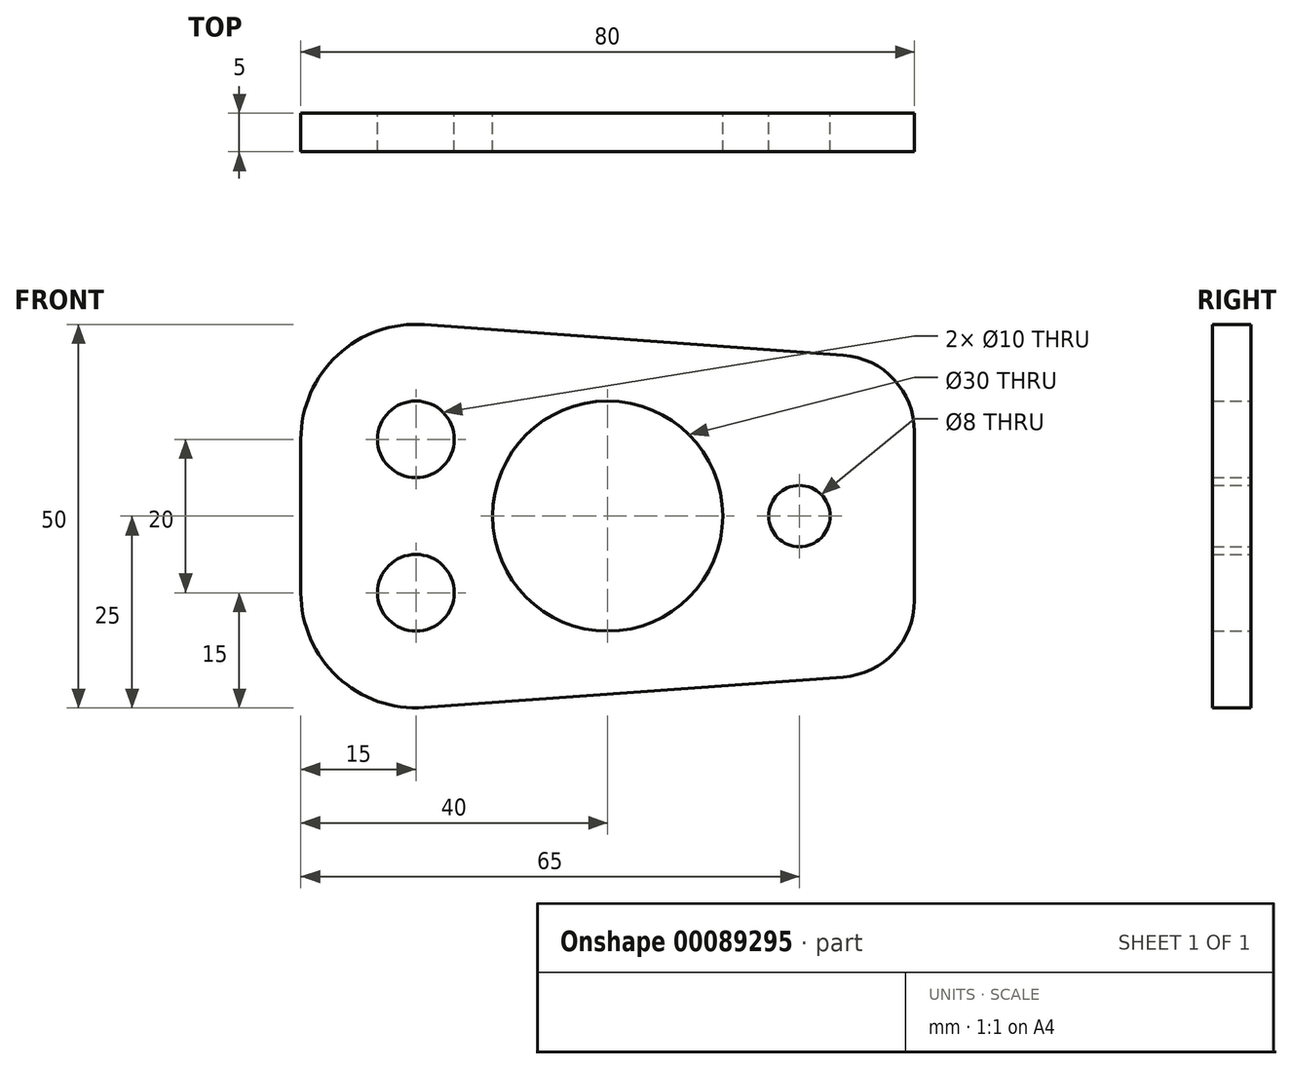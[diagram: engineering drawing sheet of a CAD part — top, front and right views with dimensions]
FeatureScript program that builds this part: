
annotation { "Feature Type Name" : "Feature", "Feature Type Description" : "" }
export const myFeature = defineFeature(function(context is Context, id is Id, definition is map)
    precondition{}
    {
        {
            var Q0;
            Q0=qCreatedBy(makeId("Front.planeOp"),FACE);
            var sketch = newSketch(context, id + "F0", { "sketchPlane" : qUnion([Q0])});
            skPoint(sketch, "E0.middle", {"position": v(0, 0) * mm});
            skCircle(sketch, "E1", {"center": v(0, 0) * mm, "radius": 15 * mm});
            skCircle(sketch, "E2", {"center": v(25, 0) * mm, "radius": 4 * mm});
            skLineSegment(sketch, "E3", {"start": v(0, 23.22) * mm, "end": v(0, -23.22) * mm, "construction": true});
            skLineSegment(sketch, "E4", {"start": v(0, 0) * mm, "end": v(40, 0) * mm, "construction": true});
            skLineSegment(sketch, "E5", {"start": v(40, 0) * mm, "end": v(-40, 0) * mm, "construction": true});
            skLineSegment(sketch, "E6", {"start": v(-40, 10) * mm, "end": v(-40, -10) * mm});
            skLineSegment(sketch, "E7", {"start": v(-23.9, -24.96) * mm, "end": v(30.73, -20.97) * mm});
            skLineSegment(sketch, "E8", {"start": v(40, -11) * mm, "end": v(40, 11) * mm});
            skLineSegment(sketch, "E9", {"start": v(30.73, 20.97) * mm, "end": v(-23.9, 24.96) * mm});
            skPoint(sketch, "E10.visualSharp", {"position": v(-40, 26.13) * mm});
            skArc(sketch, "E10.filletArc", {"start": v(-23.9, 24.96) * mm, "mid": v(-35.21, 20.99) * mm, "end": v(-40, 10) * mm});
            skPoint(sketch, "E11.visualSharp", {"position": v(-40, -26.13) * mm});
            skArc(sketch, "E11.filletArc", {"start": v(-40, -10) * mm, "mid": v(-35.21, -20.99) * mm, "end": v(-23.9, -24.96) * mm});
            skPoint(sketch, "E12.visualSharp", {"position": v(40, 20.3) * mm});
            skArc(sketch, "E12.filletArc", {"start": v(40, 11) * mm, "mid": v(37.32, 17.8) * mm, "end": v(30.73, 20.97) * mm});
            skPoint(sketch, "E13.visualSharp", {"position": v(40, -20.3) * mm});
            skArc(sketch, "E13.filletArc", {"start": v(30.73, -20.97) * mm, "mid": v(37.32, -17.8) * mm, "end": v(40, -11) * mm});
            skCircle(sketch, "E14", {"center": v(-25, 10) * mm, "radius": 5 * mm});
            skCircle(sketch, "E15", {"center": v(-25, -10) * mm, "radius": 5 * mm});
            skSolve(sketch);
        }
        {
            var Q0;
            Q0 = qSketchRegion(id + "F0", true);
            extrude(context, id + "F1", {"entities" : qUnion([Q0]), "depth" : 5 * mm});
        }
    });
